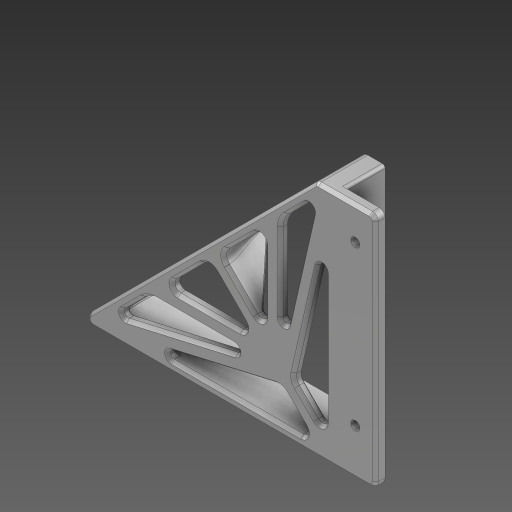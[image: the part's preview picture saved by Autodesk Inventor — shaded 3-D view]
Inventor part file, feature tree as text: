
AUTODESK INVENTOR PART (.ipt)
format: ipt  version: 2024 (Build 280153000, 153)  size: 980,480 bytes
history: native  units: mm
features: fillet x14, sketch x7, extrude x5, chamfer x5, hole x3, projected_geometry x1
ambient origin geometry x8: Origin, YZ Plane, XZ Plane, XY Plane, X Axis, Y Axis, Z Axis, Center Point
bodies: Body1 (feature_tree)
feature tree (35):
  extrude  "Extrusion3"  Depth=4.0mm
  fillet  "Fillet2"  Radius=165.0mm
  hole  "Hole4"  [1 undecoded]
  sketch  "Sketch7"  dims[d46=3.0mm]
  extrude  "Extrusion5"  Depth=10.0mm
  extrude  "Extrusion6"  Depth=5.0mm
  fillet  "Fillet4"  Radius=5.0mm
  fillet  "Fillet6"  Radius=20.0mm
  extrude  "Extrusion7"  Depth=7.5mm
  hole  "Hole6"  [1 undecoded]
  fillet  "Fillet9"  Radius=20.0mm
  fillet  "Fillet10"  Radius=5.0mm
  fillet  "Fillet11"  [1 undecoded]
  fillet  "Fillet13"  Radius=3.0mm
  fillet  "Fillet17"  Radius=3.75mm
  fillet  "Fillet19"  Radius=5.0mm
  fillet  "Fillet22"  Radius=11.0mm
  chamfer  "Chamfer5"  Distance=15.0mm
  chamfer  "Chamfer4"  Distance=62.25mm
  extrude  "Extrusion10"  Depth=10.0mm
  fillet  "Fillet23"  Radius=10.0mm
  fillet  "Fillet24"  Radius=7.62mm
  fillet  "Fillet25"  Radius=54.952633mm
  chamfer  "Chamfer9"  Distance=49.952633mm
  fillet  "Fillet27"  Radius=1.5mm
  chamfer  "Chamfer3"  Distance=8.0mm
  chamfer  "Chamfer10"  Distance=2.0mm
  hole  "Hole7"  [1 undecoded]
  sketch  "Sketch1"  dims[d3=30.0mm d41=4.0mm d42=165.0mm]
  sketch  "Sketch6"  dims[d43=45.0deg d44=5.0mm d45=0.0mm]
  sketch  "Sketch10"  dims[d47=4.5mm d48=6.0mm d49=9.4mm d50=2.0mm d51=90.0deg d52=39.95mm d53=0.0mm d54=10.0mm]
  sketch  "Sketch11"  dims[d55=80.0mm d56=23.285mm d57=5.0mm d58=20.0mm]
  sketch  "Sketch15"  dims[d61=7.5mm d63=7.5mm]
  sketch  "Sketch16"  dims[d66=3.75mm d67=7.5mm d68=20.0mm d69=0.0mm d70=5.0mm d71=0.0mm d72=0.0mm d74=3.0mm d75=3.75mm d77=5.0mm d91=11.0mm d93=15.0mm d95=62.25mm d96=15.24mm d97=10.0mm d98=0.0mm d101=6.2mm d102=6.0mm d103=9.4mm d104=2.0mm d105=90.0deg d106=8.0mm d107=0.0mm d108=7.62mm d111=54.952633mm d112=49.952633mm d115=1.5mm d116=8.0mm d117=2.0mm d124=10.0mm d131=1.0mm d132=1.4mm d133=2.0mm d134=8.726646mm d137=1.5mm d140=3.0mm d141=1.4mm d142=2.0mm d143=6.981317mm d144=20.0mm d145=2.0mm d146=8.988446mm d153=10.0mm d154=0.0mm d155=2.0mm d156=0.5mm d157=1.0mm d162=1.0mm d163=2.0mm d164=45.0deg d166=0.0mm d167=5.0mm d168=0.0mm d169=5.0mm d170=1.0mm d171=2.0mm d172=45.0deg d173=5.8mm d174=6.0mm d175=10.4mm d176=2.0mm d177=90.0deg d178=15.0mm d179=0.0mm d180=10.0mm d181=10.0mm d118=0.0mm d119=0.0mm d120=0.0mm d125=0.5mm d126=0.872665mm d127=0.5mm d128=0.872665mm d129=0.0mm d130=0.0mm]
  projected_geometry  "Project Cut Edges1"
note: 4 required parameter values undecoded (feature->parameter linkage not recoverable at this tier; creation-order binding heuristic only, values carry confidence <= 0.55)
